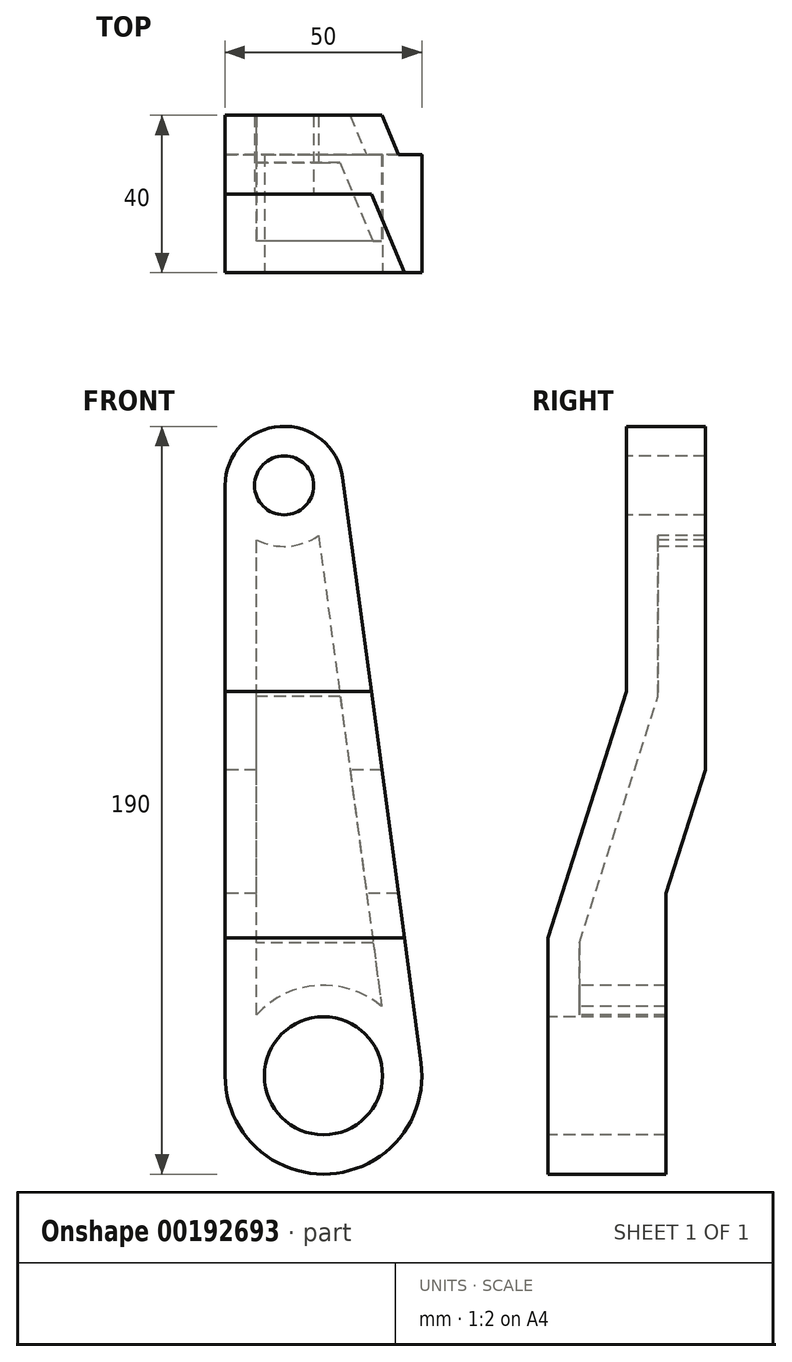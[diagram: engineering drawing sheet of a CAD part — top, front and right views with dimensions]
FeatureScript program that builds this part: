
annotation { "Feature Type Name" : "Feature", "Feature Type Description" : "" }
export const myFeature = defineFeature(function(context is Context, id is Id, definition is map)
    precondition{}
    {
        {
            var Q0;
            Q0=qCreatedBy(makeId("Front.planeOp"),FACE);
            var sketch = newSketch(context, id + "F0", { "sketchPlane" : qUnion([Q0])});
            skArc(sketch, "E0", {"start": v(-25, 0) * mm, "mid": v(1.66, -24.94) * mm, "end": v(24.78, 3.32) * mm});
            skArc(sketch, "E1", {"start": v(4.87, 152) * mm, "mid": v(-11, 164.97) * mm, "end": v(-25, 150) * mm});
            skLineSegment(sketch, "E2", {"start": v(-25, 0) * mm, "end": v(-25, 150) * mm});
            skLineSegment(sketch, "E3", {"start": v(4.87, 152) * mm, "end": v(24.78, 3.32) * mm});
            skSolve(sketch);
        }
        {
            var Q0;
            Q0 = qSketchRegion(id + "F0", true);
            extrude(context, id + "F1", {"entities" : qUnion([Q0]), "depth" : 40 * mm});
        }
        {
            var Q0;
            Q0=makeQuery(id+"F1.opExtrude","SWEPT_FACE",FACE,{"disambiguationData":[OSD([sQuery(id+"F0.wireOp",EDGE,"E2")])]});
            var sketch = newSketch(context, id + "F2", { "sketchPlane" : qUnion([Q0])});
            skLineSegment(sketch, "E4", {"start": v(20, 175) * mm, "end": v(40, 175) * mm});
            skLineSegment(sketch, "E5", {"start": v(40, 35) * mm, "end": v(20, 97.65) * mm});
            skLineSegment(sketch, "E6", {"start": v(20, 97.65) * mm, "end": v(20, 175) * mm});
            skLineSegment(sketch, "E7", {"start": v(0, -35) * mm, "end": v(10, -35) * mm});
            skLineSegment(sketch, "E8", {"start": v(10, -35) * mm, "end": v(10, 46.33) * mm});
            skLineSegment(sketch, "E9", {"start": v(10, 46.33) * mm, "end": v(0, 77.65) * mm});
            skLineSegment(sketch, "E10", {"start": v(40, 175) * mm, "end": v(40, 35) * mm});
            skLineSegment(sketch, "E11", {"start": v(0, 77.65) * mm, "end": v(0, -35) * mm});
            skSolve(sketch);
        }
        {
            var Q0;
            Q0 = qSketchRegion(id + "F2", true);
            extrude(context, id + "F3", {"entities" : qUnion([Q0]), "operationType" : NewBodyOperationType.REMOVE, "endBound" : BoundingType.THROUGH_ALL, "oppositeDirection" : true, "depth" : 3 * mm});
        }
        {
            var Q0;
            Q0=makeQuery(id+"F1.opExtrude","CAP_FACE",FACE,{"disambiguationData":[OSD([sQuery(id+"F0.wireOp",EDGE,"E0"),sQuery(id+"F0.wireOp",EDGE,"E1"),sQuery(id+"F0.wireOp",EDGE,"E2"),sQuery(id+"F0.wireOp",EDGE,"E3")])],"isStart":false});
            var sketch = newSketch(context, id + "F4", { "sketchPlane" : qUnion([Q0])});
            skCircle(sketch, "E12", {"center": v(0, 0) * mm, "radius": 15 * mm});
            skCircle(sketch, "E13", {"center": v(-10, 150) * mm, "radius": 7.5 * mm});
            skSolve(sketch);
        }
        {
            var Q0;
            Q0 = qSketchRegion(id + "F4", true);
            extrude(context, id + "F5", {"entities" : qUnion([Q0]), "operationType" : NewBodyOperationType.REMOVE, "endBound" : BoundingType.THROUGH_ALL, "oppositeDirection" : true, "depth" : 25 * mm});
        }
        {
            var Q0;
            Q0=makeQuery(id+"F1.opExtrude","CAP_FACE",FACE,{"disambiguationData":[OSD([sQuery(id+"F0.wireOp",EDGE,"E0"),sQuery(id+"F0.wireOp",EDGE,"E1"),sQuery(id+"F0.wireOp",EDGE,"E2"),sQuery(id+"F0.wireOp",EDGE,"E3")])],"isStart":true});
            var Q1;
            Q1=makeQuery(id+"F3.boolean.opBoolean","COPY",FACE,{"derivedFrom":makeQuery(id+"F3.opExtrude","SWEPT_FACE",FACE,{"disambiguationData":[OSD([sQuery(id+"F2.wireOp",EDGE,"E9")])]})});
            var Q2;
            Q2=makeQuery(id+"F3.boolean.opBoolean","COPY",FACE,{"derivedFrom":makeQuery(id+"F3.opExtrude","SWEPT_FACE",FACE,{"disambiguationData":[OSD([sQuery(id+"F2.wireOp",EDGE,"E8")])]})});
            shell(context, id + "F6", {"entities" : qUnion([Q0, Q1, Q2]), "thickness" : 8 * mm});
        }
    });
